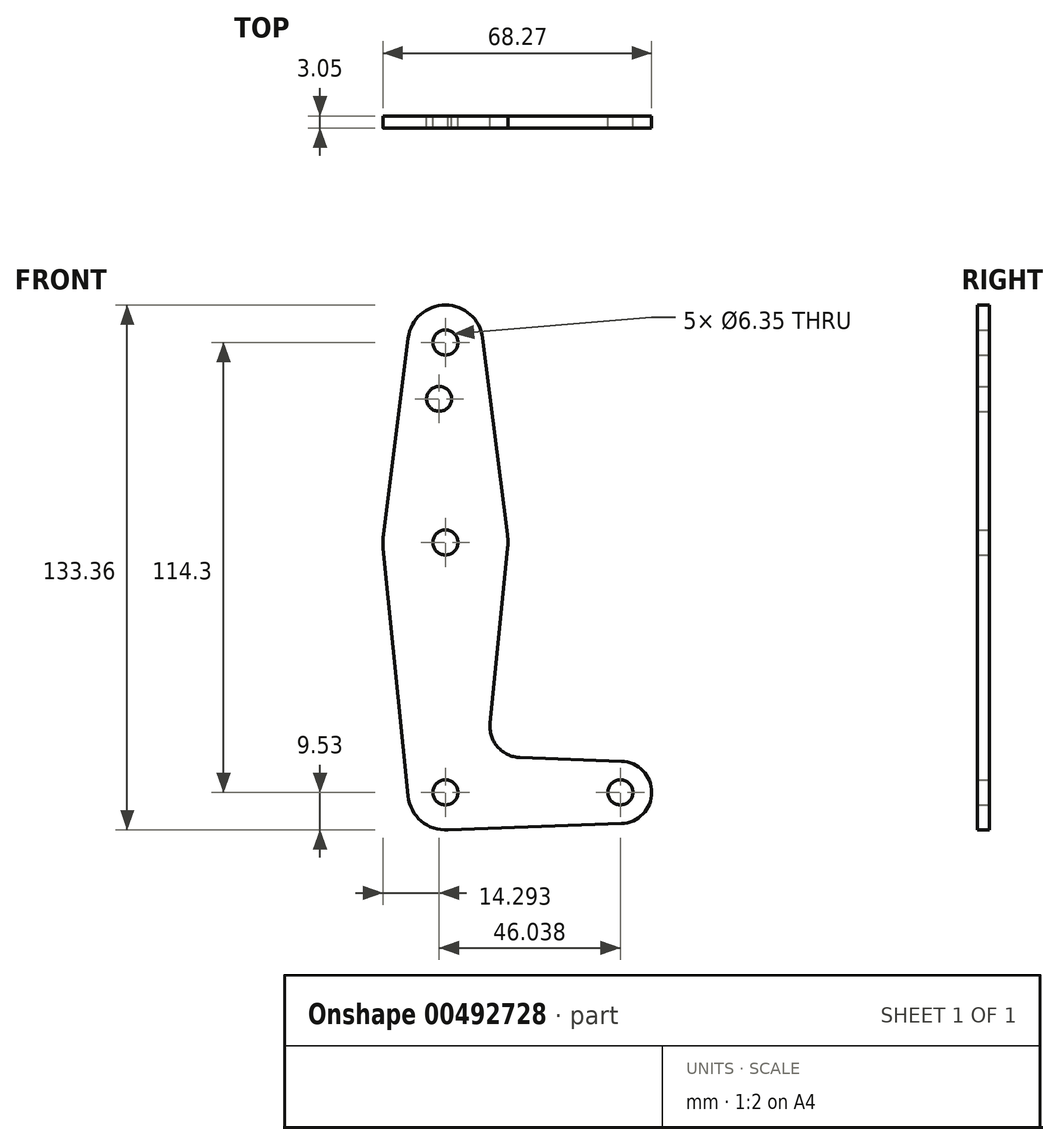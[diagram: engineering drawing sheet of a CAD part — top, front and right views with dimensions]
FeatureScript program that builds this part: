
annotation { "Feature Type Name" : "Feature", "Feature Type Description" : "" }
export const myFeature = defineFeature(function(context is Context, id is Id, definition is map)
    precondition{}
    {
        {
            var Q0;
            Q0=qCreatedBy(makeId("Front.planeOp"),FACE);
            var sketch = newSketch(context, id + "F0", { "sketchPlane" : qUnion([Q0])});
            skLineSegment(sketch, "E0", {"start": v(0, 114.3) * mm, "end": v(0, 0) * mm, "construction": true});
            skLineSegment(sketch, "E1", {"start": v(0, 0) * mm, "end": v(44.45, 0) * mm, "construction": true});
            skCircle(sketch, "E2", {"center": v(0, 0) * mm, "radius": 9.53 * mm});
            skCircle(sketch, "E3", {"center": v(0, 114.3) * mm, "radius": 9.53 * mm});
            skCircle(sketch, "E4", {"center": v(0, 63.5) * mm, "radius": 15.88 * mm});
            skCircle(sketch, "E5", {"center": v(44.45, 0) * mm, "radius": 7.94 * mm});
            skLineSegment(sketch, "E6", {"start": v(9.45, 115.5) * mm, "end": v(15.75, 65.48) * mm});
            skLineSegment(sketch, "E7", {"start": v(-9.45, 115.5) * mm, "end": v(-15.75, 65.48) * mm});
            skLineSegment(sketch, "E8", {"start": v(-15.8, 61.91) * mm, "end": v(-9.48, -0.95) * mm});
            skLineSegment(sketch, "E9", {"start": v(15.8, 61.91) * mm, "end": v(11.34, 17.6) * mm});
            skLineSegment(sketch, "E10", {"start": v(18.97, 8.86) * mm, "end": v(44.73, 7.93) * mm});
            skLineSegment(sketch, "E11", {"start": v(0, -9.53) * mm, "end": v(44.73, -7.93) * mm});
            skCircle(sketch, "E12", {"center": v(0, 114.3) * mm, "radius": 3.18 * mm});
            skCircle(sketch, "E13", {"center": v(0, 0) * mm, "radius": 3.18 * mm});
            skCircle(sketch, "E14", {"center": v(-1.59, 100) * mm, "radius": 3.18 * mm});
            skCircle(sketch, "E15", {"center": v(0, 63.5) * mm, "radius": 3.17 * mm});
            skCircle(sketch, "E16", {"center": v(44.45, 0) * mm, "radius": 3.18 * mm});
            skArc(sketch, "E17.filletArc", {"start": v(11.34, 17.6) * mm, "mid": v(13.26, 11.57) * mm, "end": v(18.97, 8.86) * mm});
            skSolve(sketch);
        }
        {
            var Q0;
            Q0 = qSketchRegion(id + "F0", true);
            extrude(context, id + "F1", {"entities" : qUnion([Q0]), "depth" : 3.05 * mm});
        }
    });
